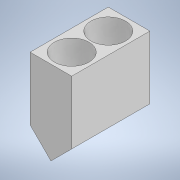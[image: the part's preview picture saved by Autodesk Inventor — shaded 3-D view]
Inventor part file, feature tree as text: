
AUTODESK INVENTOR PART (.ipt)
format: ipt  version: 2020 (Build 240168000, 168)  size: 145,920 bytes
history: native  units: mm
features: extrude x3, sketch x3
ambient origin geometry x8: Origin, YZ Plane, XZ Plane, XY Plane, X Axis, Y Axis, Z Axis, Center Point
bodies: Solid1 (feature_tree)
feature tree (6):
  extrude  "Extrusion1"  Depth=5.5mm
  extrude  "Extrusion2"  Depth=2.916667mm
  extrude  "Extrusion3"  Depth=12.4mm
  sketch  "Sketch1"  dims[d0=5.5mm d1=5.5mm]
  sketch  "Sketch2"  dims[d2=5.8mm d3=2.916667mm]
  sketch  "Sketch3"  dims[d4=3.3mm d5=3.3mm d6=3.3mm d7=3.3mm d8=10.0mm d9=0.0mm d11=45.0deg d12=45.0deg d13=12.4mm d14=0.0mm d15=1.0mm d16=1.0mm d17=1.0mm d18=1.0mm d19=2.54mm d20=2.54mm d21=1.27mm d22=1.27mm d23=4.0mm d24=0.0mm]
